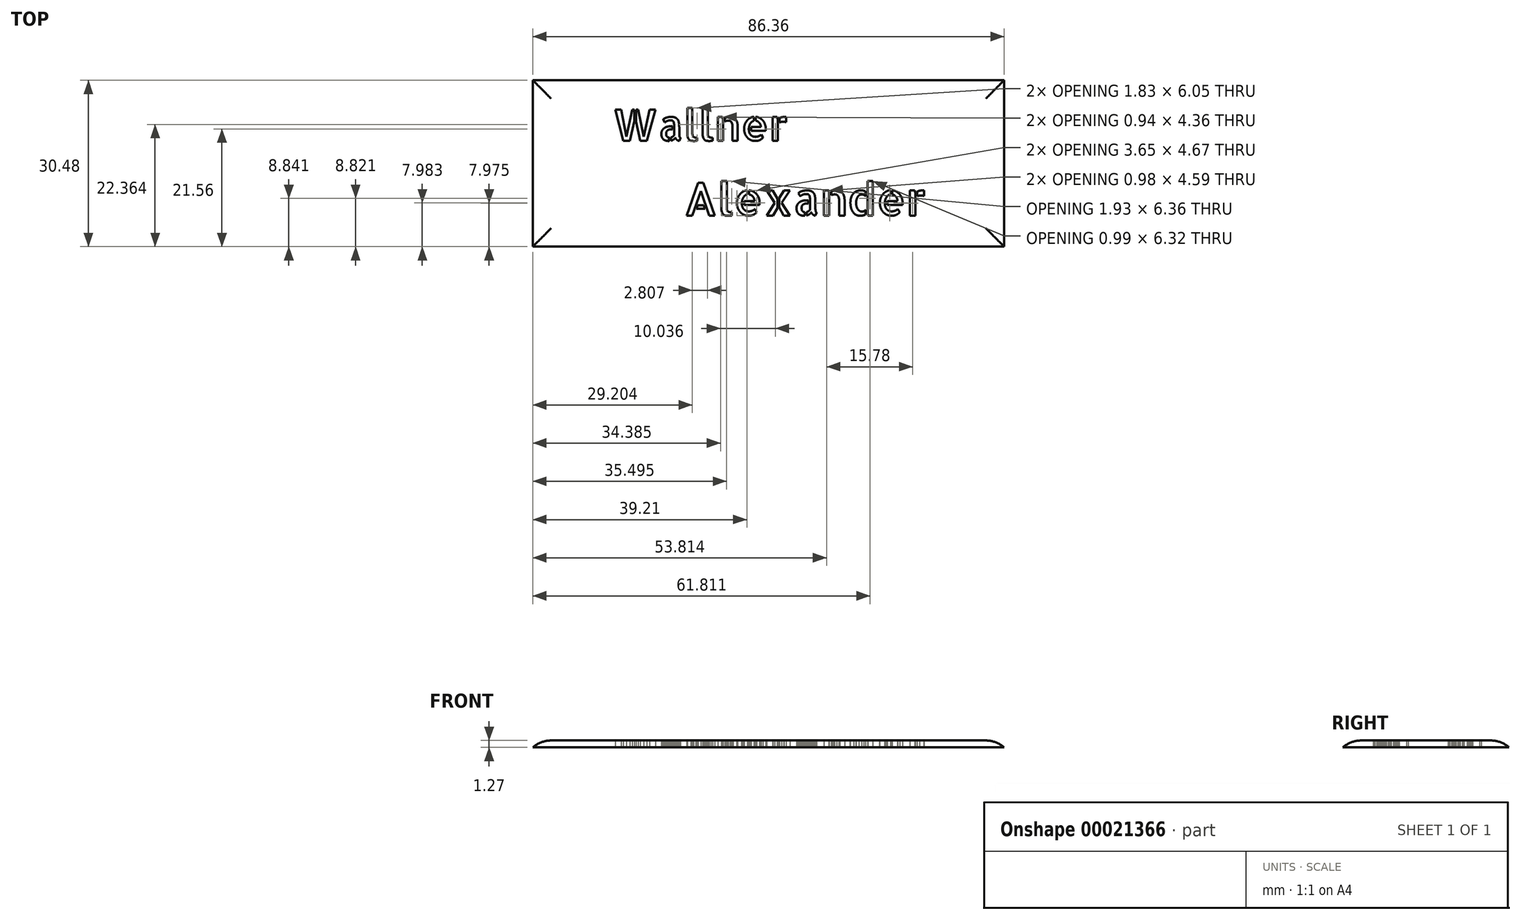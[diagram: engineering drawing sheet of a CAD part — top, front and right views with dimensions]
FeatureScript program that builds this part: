
annotation { "Feature Type Name" : "Feature", "Feature Type Description" : "" }
export const myFeature = defineFeature(function(context is Context, id is Id, definition is map)
    precondition{}
    {
        {
            var Q0;
            Q0=qCreatedBy(makeId("Top.planeOp"),FACE);
            var sketch = newSketch(context, id + "F0", { "sketchPlane" : qUnion([Q0])});
            skLineSegment(sketch, "E0.rect.bottom", {"start": v(-43.18, 15.24) * mm, "end": v(43.18, 15.24) * mm});
            skLineSegment(sketch, "E0.rect.top", {"start": v(-43.18, -15.24) * mm, "end": v(43.18, -15.24) * mm});
            skLineSegment(sketch, "E0.rect.left", {"start": v(-43.18, 15.24) * mm, "end": v(-43.18, -15.24) * mm});
            skLineSegment(sketch, "E0.rect.right", {"start": v(43.18, 15.24) * mm, "end": v(43.18, -15.24) * mm});
            skPoint(sketch, "E0.rect.middle", {"position": v(0, 0) * mm});
            skText(sketch, "E1", { "text": "Wallner", "fontName": "AllertaStencil-Regular.ttf"});
            skText(sketch, "E2", { "text": "Alexander", "fontName": "AllertaStencil-Regular.ttf"});
            const initialGuessF0  = {"E1": [-0.02863, 0.00414, 1, 0, 0.0057], "E2": [-0.01551, -0.00956, 1, 0, 0.006]};
            skSetInitialGuess(sketch, initialGuessF0);
            skSolve(sketch);
        }
        {
            var Q0;
            Q0=makeQuery(id+"F0.imprint","IMPRINT",FACE,{"disambiguationData":[TD([[makeQuery(id+"F0.imprint","IMPRINT",EDGE,{"derivedFrom":sQuery(id+"F0.wireOp",EDGE,"E0.rect.bottom")}),-1.0]])]});
            extrude(context, id + "F1", {"entities" : qUnion([Q0]), "depth" : 1.27 * mm});
        }
        {
            var Q0;
            Q0=makeQuery(id+"F1.opExtrude","CAP_EDGE",EDGE,{"disambiguationData":[OSD([sQuery(id+"F0.wireOp",EDGE,"E0.rect.bottom")])],"isStart":false});
            var Q1;
            Q1=makeQuery(id+"F1.opExtrude","CAP_EDGE",EDGE,{"disambiguationData":[OSD([sQuery(id+"F0.wireOp",EDGE,"E0.rect.right")])],"isStart":false});
            var Q2;
            Q2=makeQuery(id+"F1.opExtrude","CAP_EDGE",EDGE,{"disambiguationData":[OSD([sQuery(id+"F0.wireOp",EDGE,"E0.rect.top")])],"isStart":false});
            var Q3;
            Q3=makeQuery(id+"F1.opExtrude","CAP_EDGE",EDGE,{"disambiguationData":[OSD([sQuery(id+"F0.wireOp",EDGE,"E0.rect.left")])],"isStart":false});
            fillet(context, id + "F2", {"entities" : qUnion([Q0, Q1, Q2, Q3]), "radius" : 5.08 * mm, "tangentPropagation" : true, "allowEdgeOverflow" : false});
        }
    });
